# Revit family: PS-C43RT 1
name_source: partatom
category: Generic Models
revit_build: Autodesk Revit 2016 (Build: 20150220_1215(x64)
units: mm (PartAtom-declared; Revit-internal decimal feet)

## family parameters
Always vertical = Yes
Can host rebar = No
Cut with Voids When Loaded = No
Host = Ceiling
Part Type = Normal
Room Calculation Point = No
Round Connector Dimension = Use Diameter
Shared = No
Work Plane-Based = No

## types (1)
- Default
    100V Taps = 7.5, 15, 30
    70V Taps = 3.8, 7.5, 15, 30
    Coverage Horizontal = 120
    Coverage Vertical = 120
    Depth = 7.01
    Description = 4" 2-way Round In-ceiling Speaker with 70V/100V transformer for commercial applications
    Directivity (DI) = 8.1
    Directivity Factor (Q) = 7.6
    Frequency Range (-10dB) = 57Hz-25kHz
    Frequency Range (-3dB) = 75Hz-20kHz
    Grille = Supplied with bezel-less white grille. Optional black grille, or square adapter with black or white grille
    Height = 6.3
    High-Frequency Driver = 1” (25mm) Cloth Dome, Pivoting, Ferrofluid cooled
    Impedance = 8
    Input Connector = Four pin Euroblock with loop output connections
    Knockout = one, side-mounted 0.75"
    Low-Frequency Driver = 4” (100mm) Polypropylene Cone, Butyl Rubber Surround
    Manufacturer = Sonance
    Manufacturer URL = http://www.sonance.com
    Model = PS-C43RT
    Part Number = 40130
    Power Handling = 60
    Power Peak = 60
    Product Documentation Link = https://www.sonance.com
    Product Page URL = https://www.sonance.com
    Regulatory Compliance = UL 1480, UL 2043, NFPA 90A, NFPA 70
    SPL Max = 105
    Sensitivity = 87
    Speaker Data Link = https://www.sonance.com
    Weight Dimensional = 10.9
    Weight Product = 5.63
    Width = 6.3

## geometry (parser evidence)
native form markers: Sweep x2
no freeform markers — native parametric forms only
